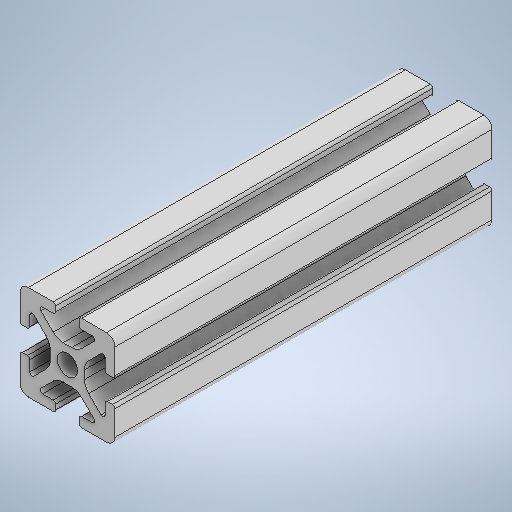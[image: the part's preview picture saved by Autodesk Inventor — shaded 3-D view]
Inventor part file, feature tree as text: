
AUTODESK INVENTOR PART (.ipt)
format: ipt  version: 2025.1 (Build 291241000, 241)  size: 325,632 bytes
history: native  units: in
note: dims shown in document units (in); Inventor stores cm internally (conversion verified against a paired STEP export)
features: direct_edit x1, mirror x1, move_body x1
ambient origin geometry x8: Origin, YZ Plane, XZ Plane, XY Plane, X Axis, Y Axis, Z Axis, Center Point
bodies: Solid1 (feature_tree)
feature tree (3):
  direct_edit  "Direct Edit1"
  mirror  "Mirror2"
  move_body  "Move1"
